# Revit family: APL Residential Thermal Heart Sliding Door SF
name_source: partatom
category: Doors
revit_build: Autodesk Revit LT 2017 (Build: 20160225_1515(x64)
units: mm (PartAtom-declared; Revit-internal decimal feet)

## family parameters
Always vertical = Yes
Cut with Voids When Loaded = No
Host = Wall
OmniClass Number = 23.30.10.00
OmniClass Title = Doors
Room Calculation Point = No
Shared = No

## types (2) — shared parameters
Analytic Construction = <None>
Arrow Opening = Yes
Frame Projection Ext. = 13 mm
Frame Projection Int. = 20 mm  [stored 0.0656168 ft]
Frame Width = 17 mm
Frame Width Sill = 15 mm  [stored 0.0492126 ft]
Function = Interior
Jamb Liner 1 = Yes
Jamb Liner 2 = Yes
Liner Head = Yes
Liner Sill = Yes
Wall Closure = By host

## per-type parameters (varying)
| type | Height | Reveal Liner | Rough Height | Rough Width | Width |
| Liner | 2201 mm | Yes | 2213 mm | 2416 mm | 2401 mm |
| Architrave | 2488 mm | No | 2500 mm  [stored 8.2021 ft] | 2500 mm  [stored 8.2021 ft] | 2485 mm |

type visibility flags (boolean, named after types; folded from table):
- Liner: Yes: (none)
- Architrave: Yes: Architrave

note: [stored X ft] marks values corroborated as IEEE doubles in the binary element streams (Revit-internal decimal feet)

## geometry (parser evidence)
native form markers: Sweep x24
no freeform markers — native parametric forms only
